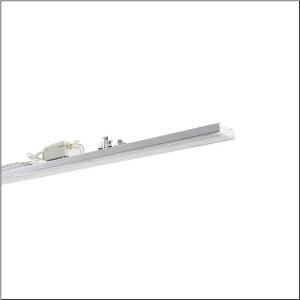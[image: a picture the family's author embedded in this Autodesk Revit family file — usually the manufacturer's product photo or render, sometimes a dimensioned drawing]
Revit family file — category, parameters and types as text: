
# Revit family: licross_r__21_recessed_mo_52te14cn485g_c326
name_source: partatom
category: Lighting Fixtures
units: mm (PartAtom-declared; Revit-internal decimal feet)

## family parameters
Cut with Voids When Loaded = No
Host = Face
Light Source = No
Part Type = Normal
Room Calculation Point = No
Round Connector Dimension = Use Diameter
Shared = No

## types (1)
- --- (1 x LED, 8530 lm, 49.9 W, 4000K)
    Apparent Load = 50 VA
    CIE Flux Codes = 56 84 97 100 100
    Color Rendering = 80
    Color Temperature = 4000K
    Default Elevation = 1800 mm
    Description = Licross® 21 Recessed MO, luminaire insert, of sheet steel, galvanised, coil coated, white, length: 1.500mm, width: 66mm, height: 67mm, LED rated luminous flux: 8.530lm, light colour: 840, control gear: ON/OFF Multilumen, CLOi, control gear: ECG DALI, with plug, 5-pole, with phase selection, mains connection: 220..240V, AC, 50/60Hz, start of lifetime: 50W, end of service life: 61W, halogen-free wiring, primary light control with lens, of plastic, primary optical cover: cover, of PMMA, light emission: direct distribution, primary light characteristic: asymmetric, protection rating (complete): IP54, insulation class (complete): insulation class I (protective earthing), certification: CE, ENEC, VDE, UKCA, protection symbol: D if used in an environment with non-conductive dust loads with corresponding accessories, impact resistance: IK06, permissible ambient temperature for indoor applications: -35..+40°C, corresponds to IFS (International Featured Standards) requirements for safety and quality in the food industry, reducing of maximum allowable ambient temperature of 5°C with ceiling mounting, LABS conformity tested according to VDMA 24364:2018-05, packaging unit: 1 piece
    Height = 58 mm
    Lamp = 1 x LED
    Lamp Light Flux = 8530 lm
    Lamp Power = 49.9 W
    Lamp count = 1
    Length = 1500 mm
    Luminous efficacy = 171 lm/W
    Manufacturer = Siteco
    ModVariant = No
    Model = 52TE14CN485G
    Mounting Place = Ceiling
    Mounting Type = Pendant
    Number of Poles = 1
    OnlyDefault = Yes
    Power Factor = 1
    Product Name = Licross® 21 Recessed MO
    Product group = luminaire insert
    ProductGroupID = 901
    Protection Class = Protection class I
    Protection Degree = IP 54
    RLX_Detail_Level = 1
    RLX_Emergency_Light_Flux = 0 lm
    RLX_Emergency_Type = 0
    RLX_Emergency_Type_DB = No
    RlxData = <blob elided: 22785 chars, md5=096bd116>
    Socket = socket
    Standby Power = 0 W
    System Light Flux = 8530 lm
    System Power = 50 W
    Type Comments = factory setting: luminous flux: 100 % | (A | C | E) | 116 mA
    Type Image = l_1296930.jpg
    URL = http://relux.com
    VarID = @adj_040849
    Voltage = 0 V
    Weight = 0.00 kg
    Width = 66 mm

## geometry (parser evidence)
native form markers: Blend x4, Sweep x11
no freeform markers — native parametric forms only
